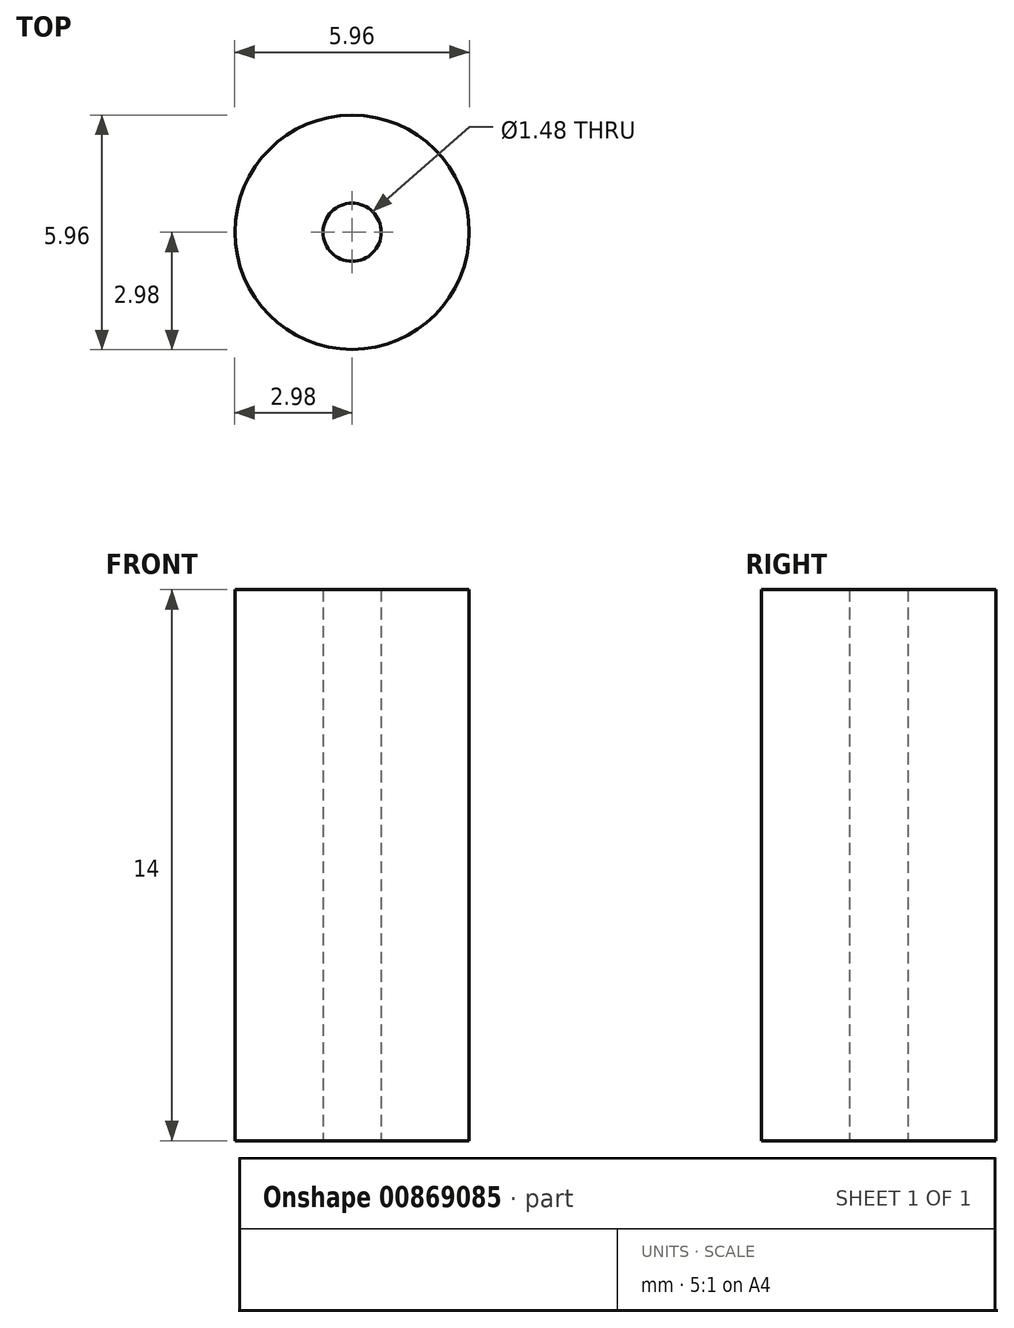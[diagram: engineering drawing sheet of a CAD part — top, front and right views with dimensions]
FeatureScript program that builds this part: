
annotation { "Feature Type Name" : "Feature", "Feature Type Description" : "" }
export const myFeature = defineFeature(function(context is Context, id is Id, definition is map)
    precondition{}
    {
        {
            var Q0;
            Q0=qCreatedBy(makeId("Top.planeOp"),FACE);
            var sketch = newSketch(context, id + "F0", { "sketchPlane" : qUnion([Q0])});
            skCircle(sketch, "E0", {"center": v(0, 0) * mm, "radius": 2.98 * mm});
            skCircle(sketch, "E1", {"center": v(0, 0) * mm, "radius": 0.74 * mm});
            skSolve(sketch);
        }
        {
            var Q0;
            Q0 = qSketchRegion(id + "F0", true);
            extrude(context, id + "F1", {"entities" : qUnion([Q0]), "depth" : 14 * mm, "offsetDistance" : 25 * mm});
        }
    });
